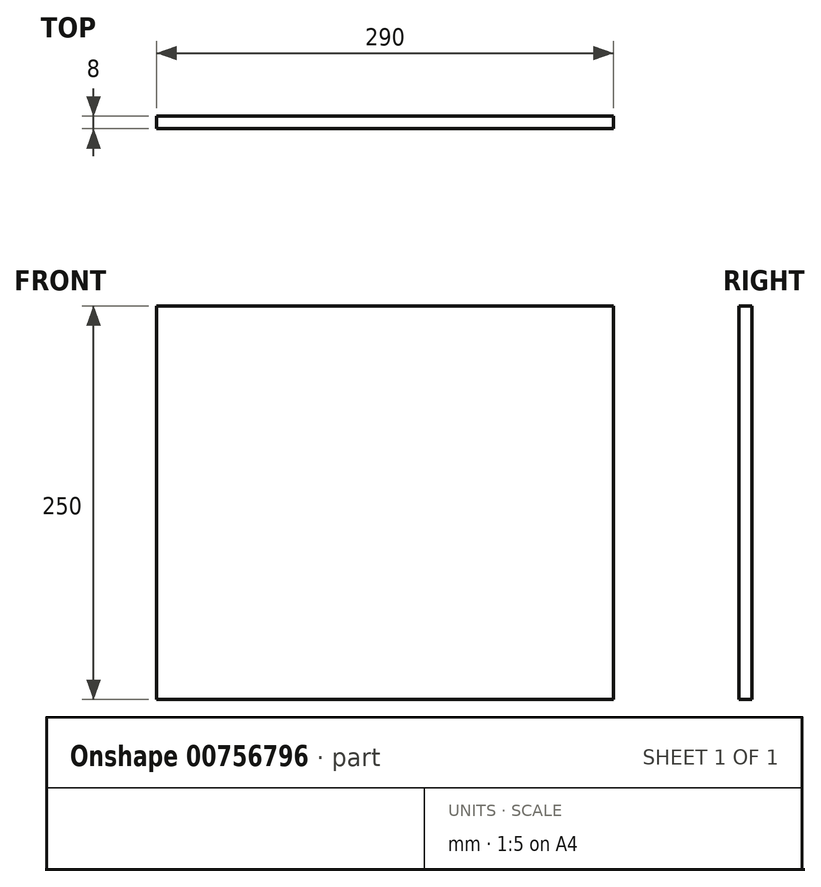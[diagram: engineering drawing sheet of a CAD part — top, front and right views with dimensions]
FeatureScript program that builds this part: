
annotation { "Feature Type Name" : "Feature", "Feature Type Description" : "" }
export const myFeature = defineFeature(function(context is Context, id is Id, definition is map)
    precondition{}
    {
        {
            var Q0;
            Q0=qCreatedBy(makeId("Front.planeOp"),FACE);
            var sketch = newSketch(context, id + "F0", { "sketchPlane" : qUnion([Q0])});
            skLineSegment(sketch, "E0.bottom", {"start": v(-283.84, 241.99) * mm, "end": v(6.16, 241.99) * mm});
            skLineSegment(sketch, "E0.top", {"start": v(-283.84, -8.01) * mm, "end": v(6.16, -8.01) * mm});
            skLineSegment(sketch, "E0.left", {"start": v(-283.84, 241.99) * mm, "end": v(-283.84, -8.01) * mm});
            skLineSegment(sketch, "E0.right", {"start": v(6.16, 241.99) * mm, "end": v(6.16, -8.01) * mm});
            skSolve(sketch);
        }
        {
            var Q0;
            Q0 = qSketchRegion(id + "F0", true);
            extrude(context, id + "F1", {"entities" : qUnion([Q0]), "depth" : 8 * mm, "offsetDistance" : 25 * mm});
        }
    });
